# Revit family: Gelenkhalter VA
name_source: partatom
category: HLS-Bauteile
revit_build: Autodesk Revit 2017 (Build: 20190507_1515(x64)
units: mm (PartAtom-declared; Revit-internal decimal feet)

## family parameters
Arbeitsebenenbasiert = Ja
Beim Laden mit Abzugskörper schneiden = Nein
Bemaßung runder Anschluss = Durchmesser verwenden
Gemeinsam genutzt = Ja
Immer vertikal = Nein
Raumberechnungspunkt = Nein
Teiletyp = Normal

## types (2) — shared parameters
Fabrikat = MEFA
Firma = MEFA Befestigungs- und Montagesysteme GmbH
Gewicht = 0.86 kg
Gewicht pro Bauteil = 0.86 kg
Kurztext2 = C-Profil längs max. Winkel 90 °
Material = Edelstahl
Vorgabe-Ansicht = 1219 mm

## per-type parameters (varying)
| type | Artikelnummer | EAN | Kurztext1 |
| Gelenkhalter V4A | 0481206 | 4250928412874 | Gelenkhalter C-Profil 45 V4A |
| Gelenkhalter V2A | 0480206 | 4250928412553 | Gelenkhalter C-Profil 45 V2A |

## geometry (parser evidence)
native form markers: Sweep x2
no freeform markers — native parametric forms only
